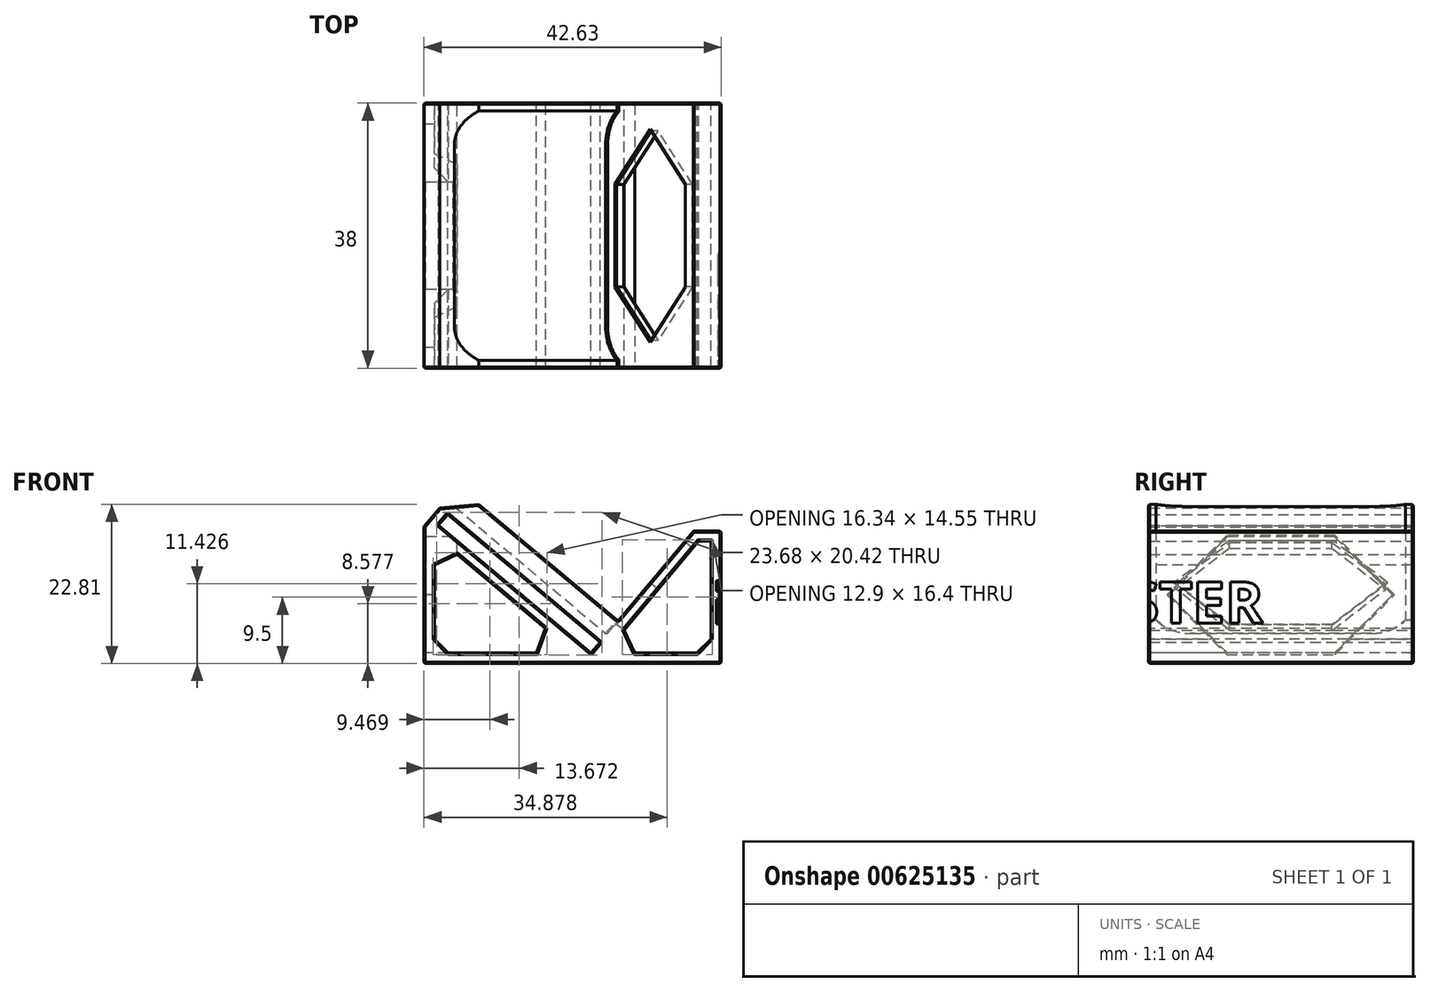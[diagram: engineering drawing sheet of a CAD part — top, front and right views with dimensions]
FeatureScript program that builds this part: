
annotation { "Feature Type Name" : "Feature", "Feature Type Description" : "" }
export const myFeature = defineFeature(function(context is Context, id is Id, definition is map)
    precondition{}
    {
        {
            var Q0;
            Q0=qCreatedBy(makeId("Front.planeOp"),FACE);
            var sketch = newSketch(context, id + "F0", { "sketchPlane" : qUnion([Q0])});
            skLineSegment(sketch, "E0", {"start": v(0, 0) * mm, "end": v(0, 19) * mm});
            skLineSegment(sketch, "E1", {"start": v(-4, 19) * mm, "end": v(-16.43, 4.18) * mm});
            skLineSegment(sketch, "E2", {"start": v(-16.43, 4.18) * mm, "end": v(-39.42, 23.46) * mm});
            skLineSegment(sketch, "E3", {"start": v(-21.02, 1.5) * mm, "end": v(-41.13, 18.38) * mm});
            skPoint(sketch, "E4", {"position": v(0, 0) * mm});
            skLineSegment(sketch, "E5", {"start": v(-39.23, 21.35) * mm, "end": v(-17.4, 3.03) * mm});
            skLineSegment(sketch, "E6", {"start": v(-17.4, 3.03) * mm, "end": v(-18.68, 1.5) * mm});
            skLineSegment(sketch, "E7", {"start": v(0, 19) * mm, "end": v(-4, 19) * mm});
            skLineSegment(sketch, "E8", {"start": v(-16.73, 1.5) * mm, "end": v(-3.3, 17.5) * mm});
            skLineSegment(sketch, "E9", {"start": v(-3.3, 17.5) * mm, "end": v(-1.5, 17.5) * mm});
            skLineSegment(sketch, "E10", {"start": v(-1.5, 17.5) * mm, "end": v(-1.5, 1.5) * mm});
            skLineSegment(sketch, "E11", {"start": v(-1.5, 1.5) * mm, "end": v(-16.73, 1.5) * mm});
            skLineSegment(sketch, "E12", {"start": v(-18.68, 1.5) * mm, "end": v(-40.52, 19.82) * mm});
            skLineSegment(sketch, "E13", {"start": v(-39.23, 21.35) * mm, "end": v(-40.52, 19.82) * mm});
            skLineSegment(sketch, "E14", {"start": v(-39.42, 23.46) * mm, "end": v(-42.63, 19.63) * mm});
            skLineSegment(sketch, "E15", {"start": v(-42.63, 19.63) * mm, "end": v(-42.63, 0) * mm});
            skLineSegment(sketch, "E16", {"start": v(-42.63, 0) * mm, "end": v(0, 0) * mm});
            skLineSegment(sketch, "E17.0", {"start": v(-41.13, 1.5) * mm, "end": v(-21.02, 1.5) * mm});
            skLineSegment(sketch, "E17.1", {"start": v(-41.13, 18.38) * mm, "end": v(-41.13, 1.5) * mm});
            skSolve(sketch);
        }
        {
            var Q0;
            {var subQ3=sQuery(id+"F0.wireOp",EDGE,"E2");Q0=makeQuery(id+"F0.imprint","IMPRINT",FACE,{"disambiguationData":[TD([[makeQuery(id+"F0.imprint","IMPRINT",EDGE,{"derivedFrom":subQ3}),1.0]])]});}
            extrude(context, id + "F1", {"entities" : qUnion([Q0]), "endBound" : BoundingType.SYMMETRIC, "depth" : 38 * mm, "offsetDistance" : 25 * mm});
        }
        {
            var Q0;
            Q0=makeQuery(id+"F1.opExtrude","SWEPT_FACE",FACE,{"disambiguationData":[OSD([sQuery(id+"F0.wireOp",EDGE,"E0")])]});
            var sketch = newSketch(context, id + "F2", { "sketchPlane" : qUnion([Q0])});
            skText(sketch, "E18", { "text": "AIRSTER", "fontName": "OpenSans-Bold.ttf"});
            skPoint(sketch, "E19", {"position": v(-17, 9.5) * mm});
            skPoint(sketch, "E20", {"position": v(-19, 9.5) * mm});
            skPoint(sketch, "E21", {"position": v(0, 19) * mm});
            const initialGuessF2  = {"E18": [-0.036, 0.00576, 1, 0, 0.00598]};
            skSetInitialGuess(sketch, initialGuessF2);
            skSolve(sketch);
        }
        {
            var Q0;
            Q0=qSketchRegion(id+"F2",true);
            extrude(context, id + "F3", {"entities" : qUnion([Q0]), "operationType" : NewBodyOperationType.REMOVE, "oppositeDirection" : true, "depth" : 0.5 * mm});
        }
        {
            var Q0;
            Q0=makeQuery(id+"F1.opExtrude","SWEPT_EDGE",EDGE,{"disambiguationData":[OSD([sQuery(id+"F0.wireOp",EDGE,"E8"),sQuery(id+"F0.wireOp",EDGE,"E11")])]});
            var Q1;
            Q1=makeQuery(id+"F1.opExtrude","SWEPT_EDGE",EDGE,{"disambiguationData":[OSD([sQuery(id+"F0.wireOp",EDGE,"E10"),sQuery(id+"F0.wireOp",EDGE,"E11")])]});
            var Q2;
            Q2=makeQuery(id+"F1.opExtrude","SWEPT_EDGE",EDGE,{"disambiguationData":[OSD([sQuery(id+"F0.wireOp",EDGE,"E17.0"),sQuery(id+"F0.wireOp",EDGE,"E17.1")])]});
            var Q3;
            Q3=makeQuery(id+"F1.opExtrude","SWEPT_EDGE",EDGE,{"disambiguationData":[OSD([sQuery(id+"F0.wireOp",EDGE,"E3"),sQuery(id+"F0.wireOp",EDGE,"E17.1")])]});
            chamfer(context, id + "F4", {"entities" : qUnion([Q0, Q1, Q2, Q3]), "width" : 2 * mm, "tangentPropagation" : true});
        }
        {
            var Q0;
            Q0=makeQuery(id+"F1.opExtrude","SWEPT_FACE",FACE,{"disambiguationData":[OSD([sQuery(id+"F0.wireOp",EDGE,"E1")])]});
            var sketch = newSketch(context, id + "F5", { "sketchPlane" : qUnion([Q0])});
            skArc(sketch, "E22", {"start": v(-19, -1.36) * mm, "mid": v(-17.24, -5.6) * mm, "end": v(-13, -7.36) * mm});
            skArc(sketch, "E23.MirrorCS", {"start": v(19, -1.36) * mm, "mid": v(17.24, -5.6) * mm, "end": v(13, -7.36) * mm});
            skLineSegment(sketch, "E24", {"start": v(-19, -4.86) * mm, "end": v(-17.87, -4.86) * mm});
            skLineSegment(sketch, "E25.MirrorCS", {"start": v(19, -4.86) * mm, "end": v(17.87, -4.86) * mm});
            skLineSegment(sketch, "E26", {"start": v(0, 9.98) * mm, "end": v(-15, 9.98) * mm});
            skLineSegment(sketch, "E27", {"start": v(-15, 9.98) * mm, "end": v(-15, -5.36) * mm});
            skLineSegment(sketch, "E28", {"start": v(-15, -5.36) * mm, "end": v(0, -5.36) * mm});
            skLineSegment(sketch, "E29.MirrorCS", {"start": v(0, 9.98) * mm, "end": v(15, 9.98) * mm});
            skLineSegment(sketch, "E30.MirrorCS", {"start": v(15, 9.98) * mm, "end": v(15, -5.36) * mm});
            skLineSegment(sketch, "E31.MirrorCS", {"start": v(15, -5.36) * mm, "end": v(0, -5.36) * mm});
            skPoint(sketch, "E32", {"position": v(-15, 2.31) * mm});
            skLineSegment(sketch, "E33", {"start": v(-15, 2.31) * mm, "end": v(-7.33, 9.98) * mm});
            skLineSegment(sketch, "E34", {"start": v(-15, 2.31) * mm, "end": v(-7.33, -5.36) * mm});
            skLineSegment(sketch, "E35.MirrorCS", {"start": v(15, 2.31) * mm, "end": v(7.33, 9.98) * mm});
            skLineSegment(sketch, "E36.MirrorCS", {"start": v(15, 2.31) * mm, "end": v(7.33, -5.36) * mm});
            skSolve(sketch);
        }
        {
            var Q0;
            {var subQ4=sQuery(id+"F5.wireOp",EDGE,"E24");Q0=makeQuery(id+"F5.imprint","IMPRINT",FACE,{"disambiguationData":[TD([[makeQuery(id+"F5.imprint","IMPRINT",EDGE,{"derivedFrom":subQ4}),-1.0]])]});}
            var Q1;
            {var subQ4=sQuery(id+"F5.wireOp",EDGE,"E25.MirrorCS");Q1=makeQuery(id+"F5.imprint","IMPRINT",FACE,{"disambiguationData":[TD([[makeQuery(id+"F5.imprint","IMPRINT",EDGE,{"derivedFrom":subQ4}),1.0]])]});}
            var Q2;
            Q2=makeQuery(id+"F1.opExtrude","SWEPT_FACE",FACE,{"disambiguationData":[OSD([sQuery(id+"F0.wireOp",EDGE,"E14")])]});
            extrude(context, id + "F6", {"entities" : qUnion([Q0, Q1]), "operationType" : NewBodyOperationType.ADD, "endBound" : BoundingType.UP_TO_SURFACE, "depth" : 25 * mm, "endBoundEntityFace" : qUnion([Q2]), "offsetDistance" : 25 * mm});
        }
        {
            var Q0;
            Q0=makeQuery(id+"F6.opExtrude","CAP_EDGE",EDGE,{"disambiguationData":[OSD([sQuery(id+"F5.wireOp",EDGE,"E24")])],"isStart":false});
            var Q1;
            Q1=makeQuery(id+"F6.opExtrude","CAP_EDGE",EDGE,{"disambiguationData":[OSD([sQuery(id+"F5.wireOp",EDGE,"E25.MirrorCS")])],"isStart":false});
            chamfer(context, id + "F7", {"entities" : qUnion([Q0, Q1]), "width" : 4 * mm, "tangentPropagation" : true});
        }
        {
            var Q0;
            {var subQ7=sQuery(id+"F5.wireOp",EDGE,"E33");Q0=makeQuery(id+"F5.imprint","IMPRINT",FACE,{"disambiguationData":[TD([[makeQuery(id+"F5.imprint","IMPRINT",EDGE,{"derivedFrom":subQ7}),-1.0]])]});}
            var Q1;
            Q1=makeQuery(id+"F1.opExtrude","SWEPT_FACE",FACE,{"disambiguationData":[OSD([sQuery(id+"F0.wireOp",EDGE,"E8")])]});
            extrude(context, id + "F8", {"entities" : qUnion([Q0]), "operationType" : NewBodyOperationType.REMOVE, "endBound" : BoundingType.UP_TO_SURFACE, "oppositeDirection" : true, "depth" : 25 * mm, "endBoundEntityFace" : qUnion([Q1]), "offsetDistance" : 25 * mm});
        }
        {
            var Q0;
            Q0=makeQuery(id+"F1.opExtrude","SWEPT_FACE",FACE,{"disambiguationData":[OSD([sQuery(id+"F0.wireOp",EDGE,"E15")])]});
            var sketch = newSketch(context, id + "F9", { "sketchPlane" : qUnion([Q0])});
            skLineSegment(sketch, "E37", {"start": v(0, 18.13) * mm, "end": v(-16, 18.13) * mm});
            skLineSegment(sketch, "E38", {"start": v(-16, 18.13) * mm, "end": v(-16, 1.5) * mm});
            skLineSegment(sketch, "E39", {"start": v(-16, 1.5) * mm, "end": v(0, 1.5) * mm});
            skPoint(sketch, "E40", {"position": v(-16, 9.82) * mm});
            skLineSegment(sketch, "E41", {"start": v(-16, 9.82) * mm, "end": v(-7.68, 18.13) * mm});
            skLineSegment(sketch, "E42", {"start": v(-16, 9.82) * mm, "end": v(-7.68, 1.5) * mm});
            skLineSegment(sketch, "E43.MirrorCS", {"start": v(0, 18.13) * mm, "end": v(16, 18.13) * mm});
            skLineSegment(sketch, "E44.MirrorCS", {"start": v(16, 9.82) * mm, "end": v(7.68, 18.13) * mm});
            skLineSegment(sketch, "E45.MirrorCS", {"start": v(16, 9.82) * mm, "end": v(7.68, 1.5) * mm});
            skLineSegment(sketch, "E46.MirrorCS", {"start": v(16, 1.5) * mm, "end": v(0, 1.5) * mm});
            skLineSegment(sketch, "E47.MirrorCS", {"start": v(16, 18.13) * mm, "end": v(16, 1.5) * mm});
            skSolve(sketch);
        }
        {
            var Q0;
            {var subQ1=sQuery(id+"F9.wireOp",EDGE,"E41");Q0=makeQuery(id+"F9.imprint","IMPRINT",FACE,{"disambiguationData":[TD([[makeQuery(id+"F9.imprint","IMPRINT",EDGE,{"derivedFrom":subQ1}),-1.0]])]});}
            var Q1;
            {var subQ0=sQuery(id+"F0.wireOp",EDGE,"E3");var subQ1=sQuery(id+"F0.wireOp",EDGE,"E17.1");Q1=makeQuery(id+"F4.opChamfer","BLEND_VERTEX",VERTEX,{"blendedFrom":[makeQuery(id+"F1.opExtrude","SWEPT_EDGE",EDGE,{"disambiguationData":[OSD([subQ0,subQ1])]}),makeQuery(id+"F1.opExtrude","CAP_FACE",FACE,{"disambiguationData":[OSD([sQuery(id+"F0.wireOp",EDGE,"E0"),sQuery(id+"F0.wireOp",EDGE,"E1"),sQuery(id+"F0.wireOp",EDGE,"E2"),subQ0,sQuery(id+"F0.wireOp",EDGE,"E5"),sQuery(id+"F0.wireOp",EDGE,"E6"),sQuery(id+"F0.wireOp",EDGE,"E7"),sQuery(id+"F0.wireOp",EDGE,"E8"),sQuery(id+"F0.wireOp",EDGE,"E9"),sQuery(id+"F0.wireOp",EDGE,"E10"),sQuery(id+"F0.wireOp",EDGE,"E11"),sQuery(id+"F0.wireOp",EDGE,"E12"),sQuery(id+"F0.wireOp",EDGE,"E13"),sQuery(id+"F0.wireOp",EDGE,"E14"),sQuery(id+"F0.wireOp",EDGE,"E15"),sQuery(id+"F0.wireOp",EDGE,"E16"),sQuery(id+"F0.wireOp",EDGE,"E17.0"),subQ1])],"isStart":true}),makeQuery(id+"F1.opExtrude","SWEPT_FACE",FACE,{"disambiguationData":[OSD([subQ0])]})],"blendedInto":[makeQuery(id+"F1.opExtrude","CAP_FACE",FACE,{"disambiguationData":[OSD([sQuery(id+"F0.wireOp",EDGE,"E0"),sQuery(id+"F0.wireOp",EDGE,"E1"),sQuery(id+"F0.wireOp",EDGE,"E2"),subQ0,sQuery(id+"F0.wireOp",EDGE,"E5"),sQuery(id+"F0.wireOp",EDGE,"E6"),sQuery(id+"F0.wireOp",EDGE,"E7"),sQuery(id+"F0.wireOp",EDGE,"E8"),sQuery(id+"F0.wireOp",EDGE,"E9"),sQuery(id+"F0.wireOp",EDGE,"E10"),sQuery(id+"F0.wireOp",EDGE,"E11"),sQuery(id+"F0.wireOp",EDGE,"E12"),sQuery(id+"F0.wireOp",EDGE,"E13"),sQuery(id+"F0.wireOp",EDGE,"E14"),sQuery(id+"F0.wireOp",EDGE,"E15"),sQuery(id+"F0.wireOp",EDGE,"E16"),sQuery(id+"F0.wireOp",EDGE,"E17.0"),subQ1])],"isStart":true}),makeQuery(id+"F1.opExtrude","SWEPT_FACE",FACE,{"disambiguationData":[OSD([subQ0])]})]});}
            extrude(context, id + "F10", {"entities" : qUnion([Q0]), "operationType" : NewBodyOperationType.REMOVE, "endBound" : BoundingType.UP_TO_VERTEX, "oppositeDirection" : true, "depth" : 25 * mm, "endBoundEntityVertex" : qUnion([Q1]), "offsetDistance" : 25 * mm});
        }
        {
            var Q0;
            Q0=makeQuery(id+"F1.opExtrude","SWEPT_EDGE",EDGE,{"disambiguationData":[OSD([sQuery(id+"F0.wireOp",EDGE,"E3"),sQuery(id+"F0.wireOp",EDGE,"E17.0")])]});
            chamfer(context, id + "F11", {"entities" : qUnion([Q0]), "width" : 2 * mm, "tangentPropagation" : true});
        }
        {
            var Q0;
            {var subQ0=sQuery(id+"F0.wireOp",EDGE,"E1");var subQ1=makeQuery(id+"F1.opExtrude","CAP_EDGE",EDGE,{"disambiguationData":[OSD([subQ0])],"isStart":false});var subQ2=sQuery(id+"F0.wireOp",EDGE,"E2");Q0=makeQuery(id+"F6.boolean.opBoolean","MERGE",FACE,{"derivedFrom":[makeQuery(id+"F1.opExtrude","CAP_FACE",FACE,{"disambiguationData":[OSD([sQuery(id+"F0.wireOp",EDGE,"E0"),subQ0,subQ2,sQuery(id+"F0.wireOp",EDGE,"E3"),sQuery(id+"F0.wireOp",EDGE,"E5"),sQuery(id+"F0.wireOp",EDGE,"E6"),sQuery(id+"F0.wireOp",EDGE,"E7"),sQuery(id+"F0.wireOp",EDGE,"E8"),sQuery(id+"F0.wireOp",EDGE,"E9"),sQuery(id+"F0.wireOp",EDGE,"E10"),sQuery(id+"F0.wireOp",EDGE,"E11"),sQuery(id+"F0.wireOp",EDGE,"E12"),sQuery(id+"F0.wireOp",EDGE,"E13"),sQuery(id+"F0.wireOp",EDGE,"E14"),sQuery(id+"F0.wireOp",EDGE,"E15"),sQuery(id+"F0.wireOp",EDGE,"E16"),sQuery(id+"F0.wireOp",EDGE,"E17.0"),sQuery(id+"F0.wireOp",EDGE,"E17.1")])],"isStart":false}),makeQuery(id+"F6.opExtrude","SWEPT_FACE",FACE,{"disambiguationData":[OSD([subQ0]),TDD([makeQuery(id+"F5.imprint","IMPRINT",EDGE,{"disambiguationData":[TD([[makeQuery(id+"F5.imprint","INTERSECT",VERTEX,{"derivedFrom":[subQ1,sQuery(id+"F5.wireOp",EDGE,"E25.MirrorCS")]}),-1.0]])],"derivedFrom":subQ1})])]})]});}
            var Q1;
            Q1=makeQuery(id+"F1.opExtrude","SWEPT_FACE",FACE,{"disambiguationData":[OSD([sQuery(id+"F0.wireOp",EDGE,"E15")])]});
            var Q2;
            {var subQ0=sQuery(id+"F0.wireOp",EDGE,"E1");var subQ1=makeQuery(id+"F1.opExtrude","CAP_EDGE",EDGE,{"disambiguationData":[OSD([subQ0])],"isStart":true});var subQ2=sQuery(id+"F0.wireOp",EDGE,"E2");Q2=makeQuery(id+"F6.boolean.opBoolean","MERGE",FACE,{"derivedFrom":[makeQuery(id+"F1.opExtrude","CAP_FACE",FACE,{"disambiguationData":[OSD([sQuery(id+"F0.wireOp",EDGE,"E0"),subQ0,subQ2,sQuery(id+"F0.wireOp",EDGE,"E3"),sQuery(id+"F0.wireOp",EDGE,"E5"),sQuery(id+"F0.wireOp",EDGE,"E6"),sQuery(id+"F0.wireOp",EDGE,"E7"),sQuery(id+"F0.wireOp",EDGE,"E8"),sQuery(id+"F0.wireOp",EDGE,"E9"),sQuery(id+"F0.wireOp",EDGE,"E10"),sQuery(id+"F0.wireOp",EDGE,"E11"),sQuery(id+"F0.wireOp",EDGE,"E12"),sQuery(id+"F0.wireOp",EDGE,"E13"),sQuery(id+"F0.wireOp",EDGE,"E14"),sQuery(id+"F0.wireOp",EDGE,"E15"),sQuery(id+"F0.wireOp",EDGE,"E16"),sQuery(id+"F0.wireOp",EDGE,"E17.0"),sQuery(id+"F0.wireOp",EDGE,"E17.1")])],"isStart":true}),makeQuery(id+"F6.opExtrude","SWEPT_FACE",FACE,{"disambiguationData":[OSD([subQ0]),TDD([makeQuery(id+"F5.imprint","IMPRINT",EDGE,{"disambiguationData":[TD([[makeQuery(id+"F5.imprint","INTERSECT",VERTEX,{"derivedFrom":[subQ1,sQuery(id+"F5.wireOp",EDGE,"E24")]}),-1.0]])],"derivedFrom":subQ1})])]})]});}
            var Q3;
            Q3=makeQuery(id+"F1.opExtrude","SWEPT_FACE",FACE,{"disambiguationData":[OSD([sQuery(id+"F0.wireOp",EDGE,"E1")])]});
            var Q4;
            Q4=makeQuery(id+"F1.opExtrude","SWEPT_EDGE",EDGE,{"disambiguationData":[OSD([sQuery(id+"F0.wireOp",EDGE,"E0"),sQuery(id+"F0.wireOp",EDGE,"E7")])]});
            var Q5;
            Q5=makeQuery(id+"F1.opExtrude","SWEPT_EDGE",EDGE,{"disambiguationData":[OSD([sQuery(id+"F0.wireOp",EDGE,"E0"),sQuery(id+"F0.wireOp",EDGE,"E16")])]});
            chamfer(context, id + "F12", {"entities" : qUnion([Q0, Q1, Q2, Q3, Q4, Q5]), "width" : 0.2 * mm, "tangentPropagation" : true});
        }
    });
